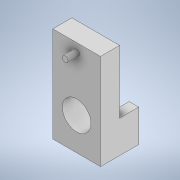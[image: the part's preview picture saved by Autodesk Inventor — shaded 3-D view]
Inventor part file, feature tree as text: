
AUTODESK INVENTOR PART (.ipt)
format: ipt  version: 2021 (Build 250183000, 183)  size: 129,536 bytes
history: native  units: mm
features: extrude x4, sketch x4, thread x1
ambient origin geometry x8: Origin, YZ Plane, XZ Plane, XY Plane, X Axis, Y Axis, Z Axis, Center Point
bodies: Solid1 (feature_tree)
feature tree (9):
  extrude  "Extrusion1"  Depth=25.0mm
  extrude  "Extrusion2"  Depth=12.5mm
  thread  "Thread1"  [1 undecoded]
  extrude  "Extrusion3"  Depth=33.0mm
  extrude  "Extrusion5"  Depth=6.0mm TaperAngle=0.0deg
  sketch  "Sketch1"  dims[d0=50.0mm d1=25.0mm]
  sketch  "Sketch2"  dims[d2=12.5mm d5=12.5mm d6=10.0mm d7=0.0mm]
  sketch  "Sketch3"  dims[d8=3.0mm d9=33.0mm]
  sketch  "Sketch5"  dims[d10=6.0mm d11=0.0mm d12=6.0mm d13=0.0mm d15=10.0mm d16=0.0mm d20=17.0mm d21=5.0mm d22=5.0mm d25=7.5mm d26=15.0mm d27=10.0mm d28=0.0mm]
note: 1 required parameter value undecoded (feature->parameter linkage not recoverable at this tier; creation-order binding heuristic only, values carry confidence <= 0.55)
